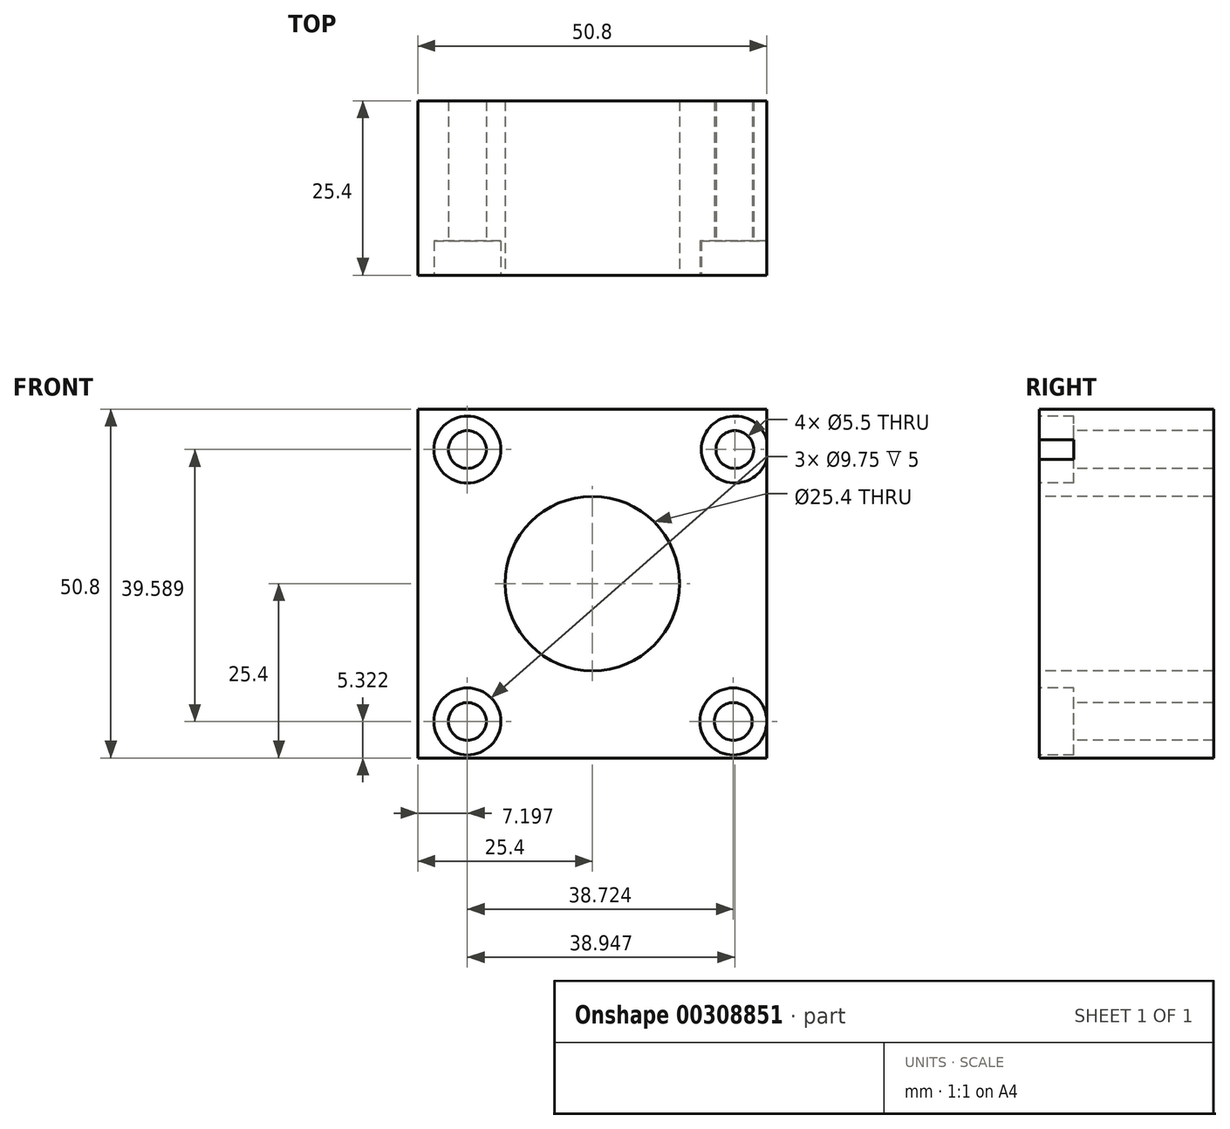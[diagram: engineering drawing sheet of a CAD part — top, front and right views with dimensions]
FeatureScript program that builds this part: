
annotation { "Feature Type Name" : "Feature", "Feature Type Description" : "" }
export const myFeature = defineFeature(function(context is Context, id is Id, definition is map)
    precondition{}
    {
        {
            var Q0;
            Q0=qCreatedBy(makeId("Front.planeOp"),FACE);
            var sketch = newSketch(context, id + "F0", { "sketchPlane" : qUnion([Q0])});
            skLineSegment(sketch, "E0.bottom", {"start": v(0, 0) * mm, "end": v(50.8, 0) * mm});
            skLineSegment(sketch, "E0.top", {"start": v(0, 50.8) * mm, "end": v(50.8, 50.8) * mm});
            skLineSegment(sketch, "E0.left", {"start": v(0, 0) * mm, "end": v(0, 50.8) * mm});
            skLineSegment(sketch, "E0.right", {"start": v(50.8, 0) * mm, "end": v(50.8, 50.8) * mm});
            skSolve(sketch);
        }
        {
            var Q0;
            Q0=makeQuery(id+"F0.imprint","IMPRINT",FACE,{"disambiguationData":[TD([[makeQuery(id+"F0.imprint","IMPRINT",EDGE,{"derivedFrom":sQuery(id+"F0.wireOp",EDGE,"E0.bottom")}),1.0]])]});
            extrude(context, id + "F1", {"entities" : qUnion([Q0]), "depth" : 25.4 * mm});
        }
        {
            var Q0;
            Q0=makeQuery(id+"F1.opExtrude","CAP_FACE",FACE,{"disambiguationData":[OSD([sQuery(id+"F0.wireOp",EDGE,"E0.bottom"),sQuery(id+"F0.wireOp",EDGE,"E0.top"),sQuery(id+"F0.wireOp",EDGE,"E0.left"),sQuery(id+"F0.wireOp",EDGE,"E0.right")])],"isStart":false});
            var sketch = newSketch(context, id + "F2", { "sketchPlane" : qUnion([Q0])});
            skCircle(sketch, "E1", {"center": v(25.4, 25.4) * mm, "radius": 12.7 * mm});
            skPoint(sketch, "E1.centerSnap0", {"position": v(50.8, 25.4) * mm});
            skPoint(sketch, "E1.centerSnap1", {"position": v(25.4, 50.8) * mm});
            skSolve(sketch);
        }
        {
            var Q0;
            Q0=makeQuery(id+"F2.imprint","IMPRINT",FACE,{"disambiguationData":[TD([[makeQuery(id+"F2.imprint","IMPRINT",EDGE,{"derivedFrom":sQuery(id+"F2.wireOp",EDGE,"E1")}),1.0]])]});
            extrude(context, id + "F3", {"entities" : qUnion([Q0]), "operationType" : NewBodyOperationType.REMOVE, "endBound" : BoundingType.THROUGH_ALL, "oppositeDirection" : true, "depth" : 25.4 * mm});
        }
        {
            var Q0;
            Q0=makeQuery(id+"F1.opExtrude","CAP_FACE",FACE,{"disambiguationData":[OSD([sQuery(id+"F0.wireOp",EDGE,"E0.bottom"),sQuery(id+"F0.wireOp",EDGE,"E0.top"),sQuery(id+"F0.wireOp",EDGE,"E0.left"),sQuery(id+"F0.wireOp",EDGE,"E0.right")])],"isStart":false});
            var sketch = newSketch(context, id + "F4", { "sketchPlane" : qUnion([Q0])});
            skPoint(sketch, "E2", {"position": v(7.2, 44.91) * mm});
            skPoint(sketch, "E3", {"position": v(46.14, 44.91) * mm});
            skPoint(sketch, "E4", {"position": v(45.92, 5.32) * mm});
            skPoint(sketch, "E5", {"position": v(7.2, 5.32) * mm});
            skSolve(sketch);
        }
        {
            var Q0;
            Q0=sQuery(id+"F4.wireOp",VERTEX,"E2");
            var Q1;
            Q1=sQuery(id+"F4.wireOp",VERTEX,"E3");
            var Q2;
            Q2=sQuery(id+"F4.wireOp",VERTEX,"E4");
            var Q3;
            Q3=sQuery(id+"F4.wireOp",VERTEX,"E5");
            var Q4;
            Q4=makeQuery(id+"F1.opExtrude","SWEPT_BODY",BODY,{"disambiguationData":[OSD([sQuery(id+"F0.wireOp",EDGE,"E0.bottom"),sQuery(id+"F0.wireOp",EDGE,"E0.top"),sQuery(id+"F0.wireOp",EDGE,"E0.left"),sQuery(id+"F0.wireOp",EDGE,"E0.right")])]});
            hole(context, id + "F5", {"style" : HoleStyle.C_BORE, "endStyle" : HoleEndStyle.THROUGH, "standardTappedOrClearance" : lookupTablePath({ "standard" : "ISO", "fit" : "Normal", "size" : "M5", "type" : "Clearance" }), "standardBlindInLast" : lookupTablePath({ "fit" : "Standard", "standard" : "ISO", "size" : "M5", "type" : "Clearance" }), "holeDiameter" : 5.5 * mm, "cBoreDiameter" : 9.75 * mm, "cBoreDepth" : 5 * mm, "tappedDepth" : 12.7 * mm, "tapClearance" : 3, "startFromSketch" : true, "locations" : qUnion([Q0, Q1, Q2, Q3]), "scope" : qUnion([Q4])});
        }
    });
